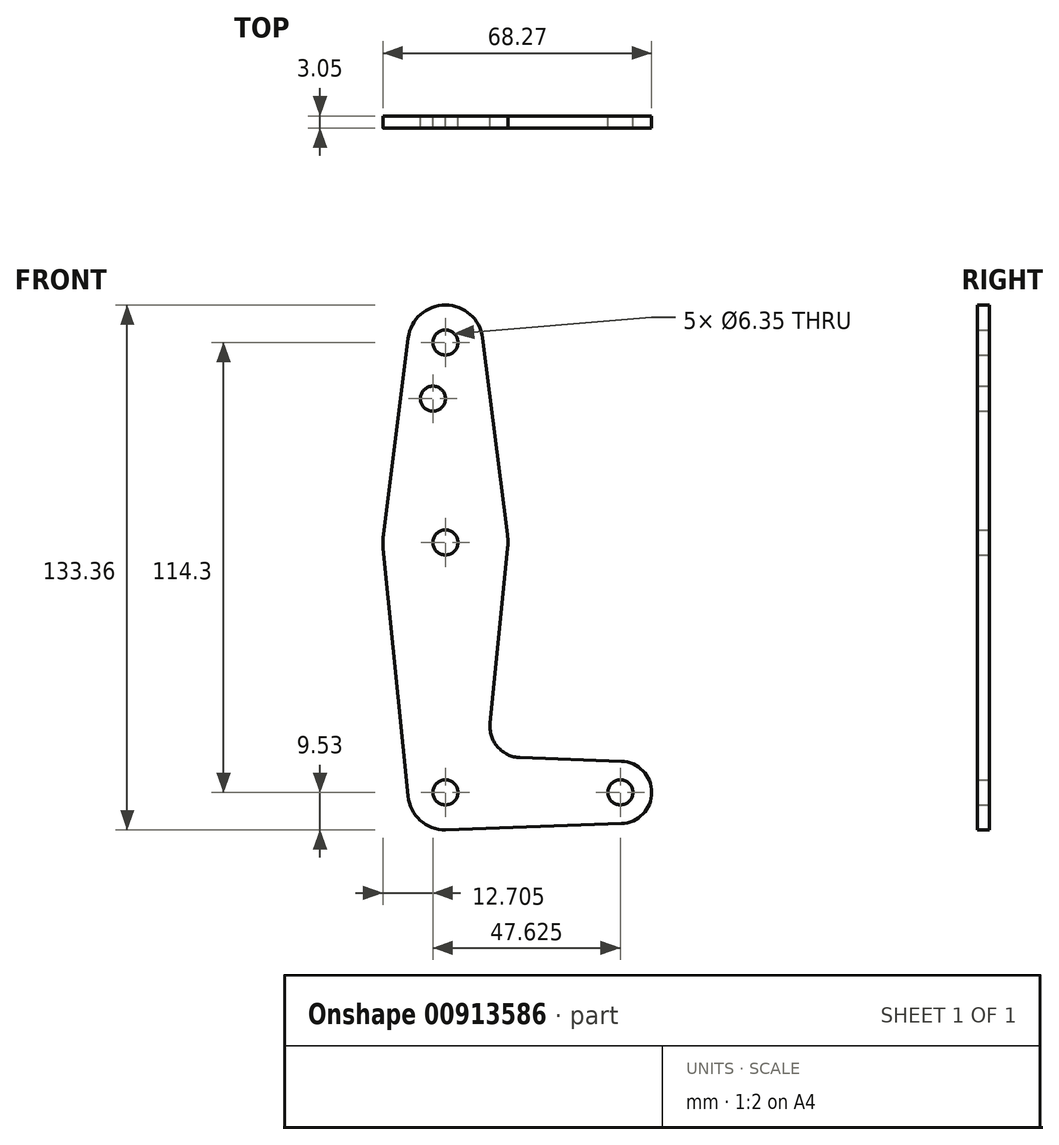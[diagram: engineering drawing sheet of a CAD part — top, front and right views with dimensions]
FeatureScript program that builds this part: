
annotation { "Feature Type Name" : "Feature", "Feature Type Description" : "" }
export const myFeature = defineFeature(function(context is Context, id is Id, definition is map)
    precondition{}
    {
        {
            var Q0;
            Q0=qCreatedBy(makeId("Front.planeOp"),FACE);
            var sketch = newSketch(context, id + "F0", { "sketchPlane" : qUnion([Q0])});
            skLineSegment(sketch, "E0", {"start": v(0, 114.3) * mm, "end": v(0, 0) * mm, "construction": true});
            skLineSegment(sketch, "E1", {"start": v(0, 0) * mm, "end": v(44.45, 0) * mm, "construction": true});
            skCircle(sketch, "E2", {"center": v(0, 114.3) * mm, "radius": 9.53 * mm});
            skCircle(sketch, "E3", {"center": v(0, 63.5) * mm, "radius": 15.88 * mm});
            skCircle(sketch, "E4", {"center": v(0, 0) * mm, "radius": 9.53 * mm});
            skCircle(sketch, "E5", {"center": v(44.45, 0) * mm, "radius": 7.94 * mm});
            skPoint(sketch, "E6", {"position": v(0, 57.15) * mm});
            skLineSegment(sketch, "E7", {"start": v(0, -9.53) * mm, "end": v(44.73, -7.93) * mm});
            skLineSegment(sketch, "E8", {"start": v(18.97, 8.85) * mm, "end": v(44.73, 7.93) * mm});
            skCircle(sketch, "E9", {"center": v(0, 114.3) * mm, "radius": 3.18 * mm});
            skCircle(sketch, "E10", {"center": v(-3.17, 100.03) * mm, "radius": 3.18 * mm});
            skCircle(sketch, "E11", {"center": v(0, 63.5) * mm, "radius": 3.18 * mm});
            skCircle(sketch, "E12", {"center": v(0, 0) * mm, "radius": 3.18 * mm});
            skCircle(sketch, "E13", {"center": v(44.45, 0) * mm, "radius": 3.18 * mm});
            skLineSegment(sketch, "E14", {"start": v(9.45, 115.5) * mm, "end": v(15.75, 65.48) * mm});
            skLineSegment(sketch, "E15", {"start": v(15.8, 61.91) * mm, "end": v(11.34, 17.59) * mm});
            skLineSegment(sketch, "E16", {"start": v(-15.8, 61.91) * mm, "end": v(-9.48, -0.95) * mm});
            skLineSegment(sketch, "E17", {"start": v(-9.45, 115.5) * mm, "end": v(-15.75, 65.48) * mm});
            skArc(sketch, "E18.filletArc", {"start": v(11.34, 17.59) * mm, "mid": v(13.26, 11.57) * mm, "end": v(18.97, 8.85) * mm});
            skSolve(sketch);
        }
        {
            var Q0;
            Q0=makeQuery(id+"F0.imprint","IMPRINT",FACE,{"disambiguationData":[TD([[makeQuery(id+"F0.imprint","IMPRINT",EDGE,{"derivedFrom":sQuery(id+"F0.wireOp",EDGE,"E10")}),-1.0]])]});
            var Q1;
            {var subQ6=sQuery(id+"F0.wireOp",EDGE,"E8");Q1=makeQuery(id+"F0.imprint","IMPRINT",FACE,{"disambiguationData":[TD([[makeQuery(id+"F0.imprint","IMPRINT",EDGE,{"derivedFrom":subQ6}),-1.0]])]});}
            var Q2;
            Q2=makeQuery(id+"F0.imprint","IMPRINT",FACE,{"disambiguationData":[TD([[makeQuery(id+"F0.imprint","IMPRINT",EDGE,{"derivedFrom":sQuery(id+"F0.wireOp",EDGE,"E11")}),-1.0]])]});
            var Q3;
            Q3=makeQuery(id+"F0.imprint","IMPRINT",FACE,{"disambiguationData":[TD([[makeQuery(id+"F0.imprint","IMPRINT",EDGE,{"derivedFrom":sQuery(id+"F0.wireOp",EDGE,"E9")}),-1.0]])]});
            var Q4;
            Q4=makeQuery(id+"F0.imprint","IMPRINT",FACE,{"disambiguationData":[TD([[makeQuery(id+"F0.imprint","IMPRINT",EDGE,{"derivedFrom":sQuery(id+"F0.wireOp",EDGE,"E12")}),-1.0]])]});
            var Q5;
            Q5=makeQuery(id+"F0.imprint","IMPRINT",FACE,{"disambiguationData":[TD([[makeQuery(id+"F0.imprint","IMPRINT",EDGE,{"derivedFrom":sQuery(id+"F0.wireOp",EDGE,"E13")}),-1.0]])]});
            extrude(context, id + "F1", {"entities" : qUnion([Q0, Q1, Q2, Q3, Q4, Q5]), "depth" : 3.05 * mm, "offsetDistance" : 25.4 * mm});
        }
        {
            var Q0;
            Q0=makeQuery(id+"F1.opExtrude","CAP_FACE",FACE,{"disambiguationData":[OSD([sQuery(id+"F0.wireOp",EDGE,"E2"),sQuery(id+"F0.wireOp",EDGE,"E3"),sQuery(id+"F0.wireOp",EDGE,"E4"),sQuery(id+"F0.wireOp",EDGE,"E5"),sQuery(id+"F0.wireOp",EDGE,"E7"),sQuery(id+"F0.wireOp",EDGE,"E8"),sQuery(id+"F0.wireOp",EDGE,"E9"),sQuery(id+"F0.wireOp",EDGE,"E10"),sQuery(id+"F0.wireOp",EDGE,"E11"),sQuery(id+"F0.wireOp",EDGE,"E12"),sQuery(id+"F0.wireOp",EDGE,"E13"),sQuery(id+"F0.wireOp",EDGE,"E14"),sQuery(id+"F0.wireOp",EDGE,"E15"),sQuery(id+"F0.wireOp",EDGE,"E16"),sQuery(id+"F0.wireOp",EDGE,"E17"),sQuery(id+"F0.wireOp",EDGE,"E18.filletArc")])],"isStart":false});
            extrude(context, id + "F2", {"entities" : qUnion([Q0]), "operationType" : NewBodyOperationType.ADD, "oppositeDirection" : true, "depth" : 2.05 * mm, "offsetDistance" : 25.4 * mm});
        }
    });
